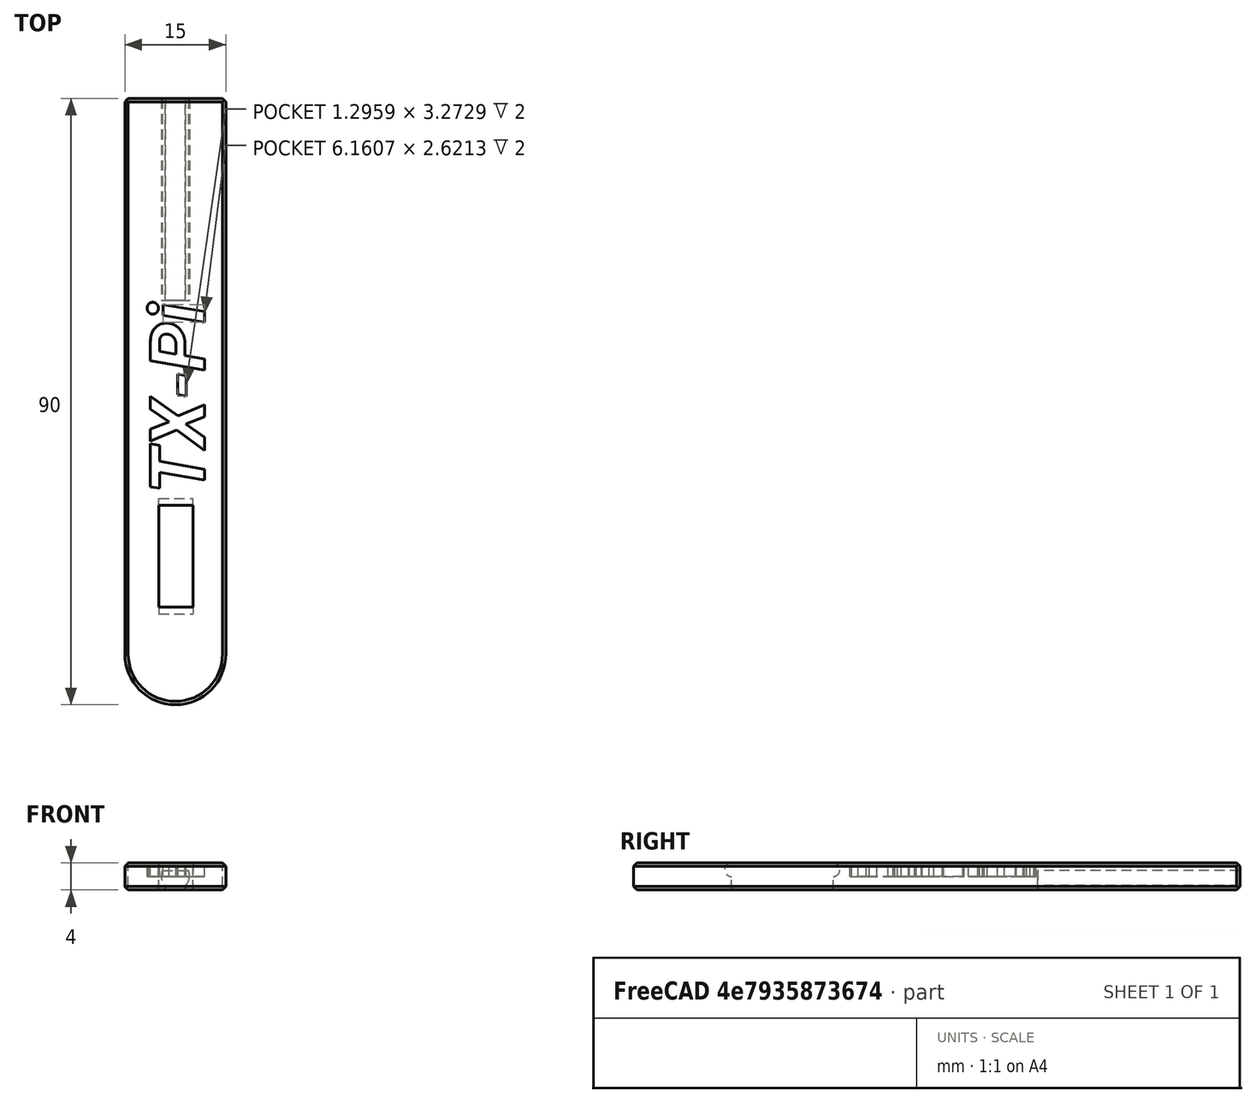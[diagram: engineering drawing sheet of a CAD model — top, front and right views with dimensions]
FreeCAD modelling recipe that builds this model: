
FCSTD DOCUMENT  (FreeCAD 0.17RUnknown)
Label: TX-Pi_stand_support_left
License: All rights reserved
LicenseURL: http://en.wikipedia.org/wiki/All_rights_reserved
objects: Part::Cut×6, Part::Box×4, Part::Cylinder×4, Part::Chamfer×3, Part::MultiFuse×2, Part::Part2DObjectPython×1, Part::Extrusion×1
note: 21 computed .brp shape members not serialized (recipe doc carries the construction recipe); baked Part::Feature solids carry a one-line shape summary decoded from their .brp

FEATURE [Part::Box] Box  label="Würfel"
  AttacherType = Attacher::AttachEngine3D
  Height = 4
  Length = 15
  Width = 82.5
FEATURE [Part::Cylinder] Cylinder  label="Zylinder"
  Angle = 360
  AttacherType = Attacher::AttachEngine3D
  Height = 4
  Placement = pos=(7.5,0,0) rot=(0,0,1;0rad)
  Radius = 7.5
FEATURE [Part::MultiFuse] Fusion
  Shapes = -> [Box,Cylinder]
FEATURE [Part::Chamfer] Chamfer
  Base = -> Fusion
  Edges = 4 edges r=0.5: [Edge3,Edge9,Edge11,Edge15]
FEATURE [Part::Chamfer] Chamfer001
  Base = -> Chamfer
  Edges = 4 edges r=0.5: [Edge3,Edge7,Edge13,Edge18]
FEATURE [Part::Chamfer] Chamfer002
  Base = -> Chamfer001
  Edges = 2 edges r=0.5: [Edge1,Edge4]
FEATURE [Part::Cylinder] Cylinder001  label="Zylinder001"
  Angle = 360
  AttacherType = Attacher::AttachEngine3D
  Height = 30
  Placement = pos=(7.5,82.5,2.1) rot=(1,0,0;1.5708rad)
  Radius = 2.1
FEATURE [Part::Box] Box001  label="Würfel001"
  AttacherType = Attacher::AttachEngine3D
  Height = 3
  Length = 4
  Placement = pos=(5.5,52.5,2.9) rot=(0,0,1;0rad)
  Width = 30
FEATURE [Part::Box] Box002  label="Würfel002"
  AttacherType = Attacher::AttachEngine3D
  Height = 3
  Length = 3
  Placement = pos=(6,52.5,-1) rot=(0,0,1;0rad)
  Width = 30
FEATURE [Part::MultiFuse] Fusion001
  Shapes = -> [Cylinder001,Box002]
FEATURE [Part::Cut] Cut
  Base = -> Fusion001
  Tool = -> Box001
FEATURE [Part::Cut] Cut001
  Base = -> Chamfer002
  Tool = -> Cut
FEATURE [Part::Box] Box003  label="Würfel003"
  AttacherType = Attacher::AttachEngine3D
  Height = 5
  Length = 5.1
  Placement = pos=(5.05,7,-0.5) rot=(0,0,1;0rad)
  Width = 15.1
FEATURE [Part::Cut] Cut002
  Base = -> Cut001
  Tool = -> Box003
FEATURE [Part::Cylinder] Cylinder002  label="Zylinder002"
  Angle = 360
  AttacherType = Attacher::AttachEngine3D
  Height = 5.1
  Placement = pos=(5.05,22.1,3) rot=(0,1,0;1.5708rad)
  Radius = 1
FEATURE [Part::Cylinder] Cylinder003  label="Zylinder003"
  Angle = 360
  AttacherType = Attacher::AttachEngine3D
  Height = 5.1
  Placement = pos=(5.05,7,3) rot=(0,1,0;1.5708rad)
  Radius = 1
FEATURE [Part::Cut] Cut003
  Base = -> Cut002
  Tool = -> Cylinder002
FEATURE [Part::Cut] Cut004
  Base = -> Cut003
  Tool = -> Cylinder003
FEATURE [Part::Part2DObjectPython] ShapeString  # Draft 2D object (typed FeaturePython)
  FontFile = <path>
  Placement = pos=(-9.1754,-3.35448,0) rot=(0,0,1;0rad)
  Size = 10
  String = TX-Pi
  Tracking = 0
FEATURE [Part::Extrusion] Extrude
  Base = -> ShapeString
  Dir = (0,0,7)
  DirMode = 0
  FaceMakerClass = Part::FaceMakerExtrusion
  LengthFwd = 0
  LengthRev = 0
  Placement = pos=(8.5,33,2) rot=(0,0,1;1.5708rad)
  Solid = true
  Symmetric = false
FEATURE [Part::Cut] Cut005
  Base = -> Cut004
  Tool = -> Extrude
note: 1 file-system path scrubbed to <path> (originals preserved in the JSON sidecar)
